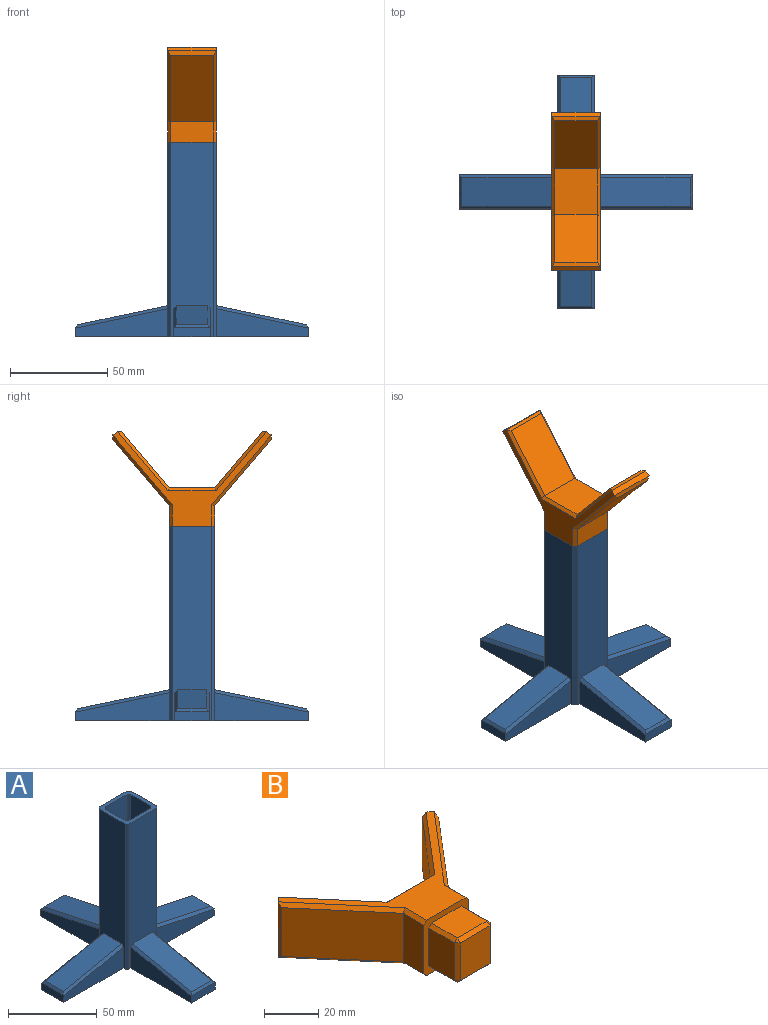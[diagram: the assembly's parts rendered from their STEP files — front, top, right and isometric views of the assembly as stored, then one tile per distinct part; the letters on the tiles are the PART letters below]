
ASSEMBLY  parts=2 mates=1
PART A: 47 faces, bbox 120x120x100 mm
  f0: plane 100x22mm, normal (0,-1,0), area 1898.3mm2, adj f2,f5,f16,f17,f24,f25,f26,f44
  f1: plane 100x22mm, normal (0,1,0), area 1898.3mm2, adj f2,f5,f15,f18,f20,f21,f22,f35
  f2: plane 25x23.5mm, normal (0,0,1), area 209.8mm2, adj f0,f1,f3,f4,f6,f7,f8,f9
  f3: plane 100x20.5mm, normal (-1,0,0), area 1772.3mm2, adj f2,f5,f15,f16,f28,f29,f30,f38
  f4: plane 100x20.5mm, normal (1,0,0), area 1772.3mm2, adj f2,f5,f17,f18,f32,f33,f34,f41
  f5: plane 120x120mm, normal (0,0,-1), area 4079mm2, adj f0,f1,f3,f4,f15,f16,f17,f18
  f6: plane 25x17.2mm, normal (0,-1,0), area 430mm2, adj f2,f10,f11,f14
  f7: plane 25x15.7mm, normal (1,0,0), area 392.5mm2, adj f2,f10,f13,f14
  f8: plane 25x17.2mm, normal (0,1,0), area 430mm2, adj f2,f10,f12,f13
  f9: plane 25x15.7mm, normal (-1,0,0), area 392.5mm2, adj f2,f10,f11,f12
  f10: plane 20.2x18.7mm, normal (0,0,1), area 373.2mm2, adj f6,f7,f8,f9,f11,f12,f13,f14
  f11: plane 25x1.5mm, normal (-0.71,-0.71,0), area 53mm2, adj f2,f6,f9,f10
  f12: plane 25x1.5mm, normal (-0.71,0.71,0), area 53mm2, adj f2,f8,f9,f10
  f13: plane 25x1.5mm, normal (0.71,0.71,0), area 53mm2, adj f2,f7,f8,f10
  f14: plane 25x1.5mm, normal (0.71,-0.71,0), area 53mm2, adj f2,f6,f7,f10
  f15: plane 100x1.5mm, normal (-0.71,0.71,0), area 212.1mm2, adj f1,f2,f3,f5
  f16: plane 100x1.5mm, normal (-0.71,-0.71,0), area 212.1mm2, adj f0,f2,f3,f5
  f17: plane 100x1.5mm, normal (0.71,-0.71,0), area 212.1mm2, adj f0,f2,f4,f5
  f18: plane 100x1.5mm, normal (0.71,0.71,0), area 212.1mm2, adj f1,f2,f4,f5
  f19: plane 19x4.78mm, normal (0,1,0), area 90.7mm2, adj f5,f21,f22,f35,f36,f37
  f20: plane 47.05x16mm, normal (0,0.2,0.98), area 768.9mm2, adj f1,f35,f36,f37
  f21: plane 48.25x14.47mm, normal (1,0,0), area 456.8mm2, adj f1,f5,f19,f35
  f22: plane 48.25x14.47mm, normal (-1,0,0), area 456.8mm2, adj f1,f5,f19,f36
  f23: plane 19x4.78mm, normal (0,-1,0), area 90.7mm2, adj f5,f25,f26,f44,f45,f46
  f24: plane 47.05x16mm, normal (0,-0.2,0.98), area 768.9mm2, adj f0,f44,f45,f46
  f25: plane 48.25x14.47mm, normal (1,0,0), area 456.8mm2, adj f0,f5,f23,f44
  f26: plane 48.25x14.47mm, normal (-1,0,0), area 456.8mm2, adj f0,f5,f23,f45
  f27: plane 17.5x4.78mm, normal (-1,0,0), area 83.6mm2, adj f5,f29,f30,f38,f39,f40
  f28: plane 46.31x14.5mm, normal (-0.21,0,0.98), area 686.2mm2, adj f3,f38,f39,f40
  f29: plane 47.5x14.47mm, normal (0,-1,0), area 449.7mm2, adj f3,f5,f27,f38
  f30: plane 47.5x14.47mm, normal (0,1,0), area 449.7mm2, adj f3,f5,f27,f39
  f31: plane 17.5x4.78mm, normal (1,0,0), area 83.6mm2, adj f5,f33,f34,f41,f42,f43
  f32: plane 46.31x14.5mm, normal (0.21,0,0.98), area 686.2mm2, adj f4,f41,f42,f43
  f33: plane 47.5x14.47mm, normal (0,-1,0), area 449.7mm2, adj f4,f5,f31,f41
  f34: plane 47.5x14.47mm, normal (0,1,0), area 449.7mm2, adj f4,f5,f31,f42
  f35: plane 48.25x11.53mm, normal (0.71,0.14,0.69), area 103.5mm2, adj f1,f19,f20,f21,f37
  f36: plane 48.25x11.53mm, normal (-0.71,0.14,0.69), area 103.5mm2, adj f1,f19,f20,f22,f37
  f37: plane 18.39x1.47mm, normal (0,0.78,0.63), area 32.6mm2, adj f19,f20,f35,f36
  f38: plane 47.5x11.53mm, normal (-0.15,-0.71,0.69), area 101.9mm2, adj f3,f27,f28,f29,f40
  f39: plane 47.5x11.53mm, normal (-0.15,0.71,0.69), area 101.9mm2, adj f3,f27,f28,f30,f40
  f40: plane 16.88x1.47mm, normal (-0.78,0,0.63), area 29.7mm2, adj f27,f28,f38,f39
  f41: plane 47.5x11.53mm, normal (0.15,-0.71,0.69), area 101.9mm2, adj f4,f31,f32,f33,f43
  f42: plane 47.5x11.53mm, normal (0.15,0.71,0.69), area 101.9mm2, adj f4,f31,f32,f34,f43
  f43: plane 16.88x1.47mm, normal (0.78,0,0.63), area 29.7mm2, adj f31,f32,f41,f42
  f44: plane 48.25x11.53mm, normal (0.71,-0.14,0.69), area 103.5mm2, adj f0,f23,f24,f25,f46
  f45: plane 48.25x11.53mm, normal (-0.71,-0.14,0.69), area 103.5mm2, adj f0,f23,f24,f26,f46
  f46: plane 18.39x1.47mm, normal (0,-0.78,0.63), area 32.6mm2, adj f23,f24,f44,f45
PART B: 47 faces, bbox 81.7x64x25 mm
  f0: plane 28.86x24.53mm, normal (0.76,0.65,0), area 833.3mm2, adj f5,f14,f16,f18
  f1: plane 25x2.29mm, normal (-0.65,0.76,0), area 75mm2, adj f6,f7,f16,f22
  f2: plane 34.23x29.11mm, normal (-0.76,-0.65,0), area 988.6mm2, adj f3,f21,f22,f23
  f3: plane 22x10.74mm, normal (-1,0,0), area 236.2mm2, adj f2,f4,f20,f24
  f4: plane 25x23.5mm, normal (0,-1,0), area 217.5mm2, adj f3,f6,f7,f11,f20,f24,f25,f29
  f5: plane 23.5x22mm, normal (0,1,0), area 517mm2, adj f0,f8,f12,f19
  f6: plane 81.37x49.03mm, normal (0,0,1), area 656.2mm2, adj f1,f4,f9,f12,f13,f14,f20,f21
  f7: plane 81.37x49.03mm, normal (0,0,-1), area 656.2mm2, adj f1,f4,f9,f17,f18,f19,f23,f24
  f8: plane 28.86x24.53mm, normal (-0.76,0.65,0), area 833.3mm2, adj f5,f13,f15,f17
  f9: plane 25x2.29mm, normal (0.65,0.76,0), area 75mm2, adj f6,f7,f15,f27
  f10: plane 34.23x29.11mm, normal (0.76,-0.65,0), area 988.6mm2, adj f11,f26,f27,f28
  f11: plane 22x10.74mm, normal (1,0,0), area 236.2mm2, adj f4,f10,f25,f29
  f12: plane 24.89x1.5mm, normal (0,0.71,0.71), area 51.3mm2, adj f5,f6,f13,f14
  f13: plane 30.53x26.65mm, normal (-0.54,0.46,0.71), area 82.7mm2, adj f6,f8,f12,f15
  f14: plane 30.53x26.65mm, normal (0.54,0.46,0.71), area 82.7mm2, adj f0,f6,f12,f16
  f15: plane 25x2.11mm, normal (-0.08,1,0), area 49.9mm2, adj f8,f9,f13,f17
  f16: plane 25x2.11mm, normal (0.08,1,0), area 49.9mm2, adj f0,f1,f14,f18
  f17: plane 30.53x26.65mm, normal (-0.54,0.46,-0.71), area 82.7mm2, adj f7,f8,f15,f19
  f18: plane 30.53x26.65mm, normal (0.54,0.46,-0.71), area 82.7mm2, adj f0,f7,f16,f19
  f19: plane 24.89x1.5mm, normal (0,0.71,-0.71), area 51.3mm2, adj f5,f7,f17,f18
  f20: plane 11.29x1.5mm, normal (-0.71,0,0.71), area 23.4mm2, adj f3,f4,f6,f21
  f21: plane 36.35x30.61mm, normal (-0.54,-0.46,0.71), area 97.5mm2, adj f2,f6,f20,f22
  f22: plane 25x2.11mm, normal (-1,0.08,0), area 49.9mm2, adj f1,f2,f21,f23
  f23: plane 36.35x30.61mm, normal (-0.54,-0.46,-0.71), area 97.5mm2, adj f2,f7,f22,f24
  f24: plane 11.29x1.5mm, normal (-0.71,0,-0.71), area 23.4mm2, adj f3,f4,f7,f23
  f25: plane 11.29x1.5mm, normal (0.71,0,0.71), area 23.4mm2, adj f4,f6,f11,f26
  f26: plane 36.35x30.61mm, normal (0.54,-0.46,0.71), area 97.5mm2, adj f6,f10,f25,f27
  f27: plane 25x2.11mm, normal (1,0.08,0), area 49.9mm2, adj f9,f10,f26,f28
  f28: plane 36.35x30.61mm, normal (0.54,-0.46,-0.71), area 97.5mm2, adj f7,f10,f27,f29
  f29: plane 11.29x1.5mm, normal (0.71,0,-0.71), area 23.4mm2, adj f4,f7,f11,f28
  f30: plane 17x13.5mm, normal (1,0,0), area 229.5mm2, adj f4,f35,f40,f41
  f31: plane 15.5x13.5mm, normal (0,0,1), area 209.3mm2, adj f4,f40,f43,f46
  f32: plane 17x13.5mm, normal (-1,0,0), area 229.5mm2, adj f4,f37,f42,f43
  f33: plane 15.5x13.5mm, normal (0,0,-1), area 209.3mm2, adj f4,f35,f36,f37
  f34: plane 17x15.5mm, normal (0,-1,0), area 263.5mm2, adj f36,f41,f42,f46
  f35: plane 13.5x1.5mm, normal (0.71,0,-0.71), area 28.6mm2, adj f4,f30,f33,f38
  f36: plane 15.5x1.5mm, normal (0,-0.71,-0.71), area 32.9mm2, adj f33,f34,f38,f39
  f37: plane 13.5x1.5mm, normal (-0.71,0,-0.71), area 28.6mm2, adj f4,f32,f33,f39
  f38: plane 1.5x1.5mm, normal (0.58,-0.58,-0.58), area 1.9mm2, adj f35,f36,f41
  f39: plane 1.5x1.5mm, normal (-0.58,-0.58,-0.58), area 1.9mm2, adj f36,f37,f42
  f40: plane 13.5x1.5mm, normal (0.71,0,0.71), area 28.6mm2, adj f4,f30,f31,f44
  f41: plane 17x1.5mm, normal (0.71,-0.71,0), area 36.1mm2, adj f30,f34,f38,f44
  f42: plane 17x1.5mm, normal (-0.71,-0.71,0), area 36.1mm2, adj f32,f34,f39,f45
  f43: plane 13.5x1.5mm, normal (-0.71,0,0.71), area 28.6mm2, adj f4,f31,f32,f45
  f44: plane 1.5x1.5mm, normal (0.58,-0.58,0.58), area 1.9mm2, adj f40,f41,f46
  f45: plane 1.5x1.5mm, normal (-0.58,-0.58,0.58), area 1.9mm2, adj f42,f43,f46
  f46: plane 15.5x1.5mm, normal (0,-0.71,0.71), area 32.9mm2, adj f31,f34,f44,f45
PLACE A at identity fixed
PLACE B rot(axis=(0.58,0.58,0.58),120deg) t=(-12.5,0,165)mm
MATE fastened B.f4 <-> A.f2  axis (0,0,1) through (0,0,100)mm
